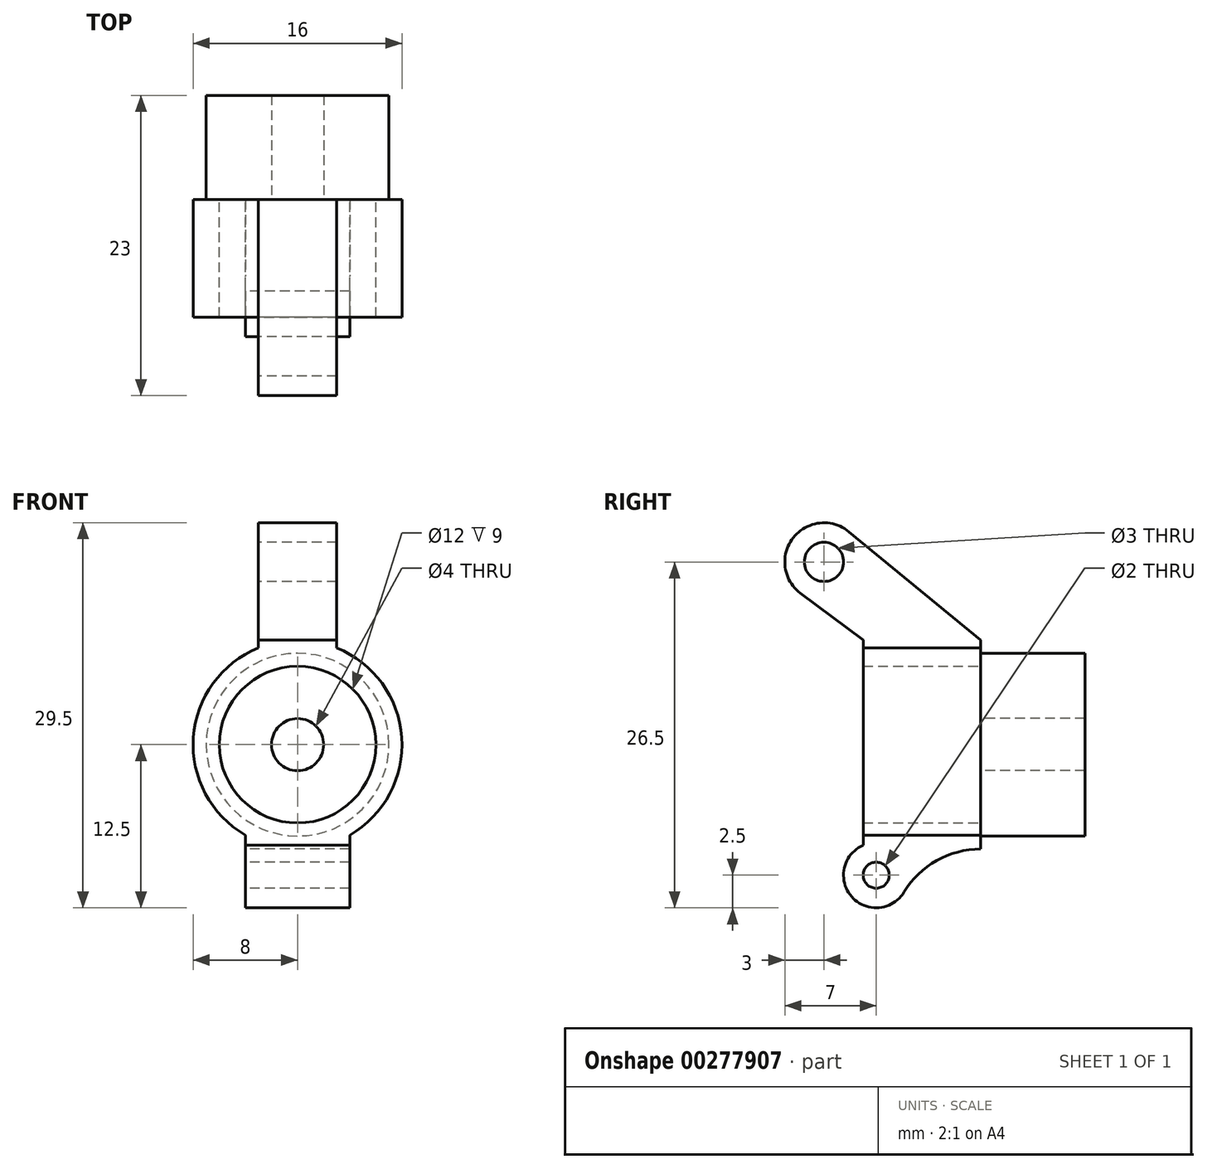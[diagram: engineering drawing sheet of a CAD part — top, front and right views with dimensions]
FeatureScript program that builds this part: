
annotation { "Feature Type Name" : "Feature", "Feature Type Description" : "" }
export const myFeature = defineFeature(function(context is Context, id is Id, definition is map)
    precondition{}
    {
        {
            var Q0;
            Q0=qCreatedBy(makeId("Front.planeOp"),FACE);
            var sketch = newSketch(context, id + "F0", { "sketchPlane" : qUnion([Q0])});
            skArc(sketch, "E0", {"start": v(8, 0) * mm, "mid": v(0, 8) * mm, "end": v(-8, 0) * mm});
            skCircle(sketch, "E1", {"center": v(0, 0) * mm, "radius": 6 * mm});
            skLineSegment(sketch, "E2", {"start": v(0, 0) * mm, "end": v(9.88, 0) * mm, "construction": true});
            skLineSegment(sketch, "E3", {"start": v(0, 0) * mm, "end": v(0, 9.34) * mm, "construction": true});
            skLineSegment(sketch, "E4.MirrorCS", {"start": v(0, 0) * mm, "end": v(-9.88, 0) * mm, "construction": true});
            skArc(sketch, "E5.trimOffspring", {"start": v(-8, 0) * mm, "mid": v(0, -8) * mm, "end": v(8, 0) * mm});
            skPoint(sketch, "E6.end.orphan", {"position": v(7.5, 4) * mm});
            skPoint(sketch, "E6.start.orphan", {"position": v(8, 0) * mm});
            skPoint(sketch, "E7.MirrorCS.end.orphan", {"position": v(7.5, -4) * mm});
            skPoint(sketch, "E8.MirrorCS.start.orphan", {"position": v(-8, 0) * mm});
            skPoint(sketch, "E9.MirrorCS.start.orphan", {"position": v(-7.5, 4) * mm});
            skPoint(sketch, "E10.MirrorCS.start.orphan", {"position": v(-7.5, -4) * mm});
            skSolve(sketch);
        }
        {
            var Q0;
            Q0=qSketchRegion(id+"F0",true);
            extrude(context, id + "F1", {"entities" : qUnion([Q0]), "depth" : 9 * mm, "symmetric" : true});
        }
        {
            var Q0;
            Q0=makeQuery(id+"FDlZR3japZBE9mr_1.boolean.opBoolean","MERGE",FACE,{"derivedFrom":[makeQuery(id+"F1.opExtrude","CAP_FACE",FACE,{"disambiguationData":[OSD([sQuery(id+"F0.wireOp",EDGE,"E0"),sQuery(id+"F0.wireOp",EDGE,"E1"),sQuery(id+"F0.wireOp",EDGE,"E6"),sQuery(id+"F0.wireOp",EDGE,"bKShqBVs-TCg5-hqsg-2Zin-jb4kYLIbsAUQ"),sQuery(id+"F0.wireOp",EDGE,"E8.MirrorCS"),sQuery(id+"F0.wireOp",EDGE,"E9.MirrorCS"),sQuery(id+"F0.wireOp",EDGE,"E7.MirrorCS"),sQuery(id+"F0.wireOp",EDGE,"0079e600-e878-4d57-aa4f-ef33ea1a4fac0.MirrorCS"),sQuery(id+"F0.wireOp",EDGE,"f6fc4373-7105-42fd-a591-3c9390de6fbc0.MirrorCS"),sQuery(id+"F0.wireOp",EDGE,"E10.MirrorCS"),sQuery(id+"F0.wireOp",EDGE,"E5.trimOffspring")])],"isStart":true}),makeQuery(id+"FDlZR3japZBE9mr_1.opExtrude","SWEPT_FACE",FACE,{"disambiguationData":[OSD([sQuery(id+"FTksZrnYcWv5Ukm_1.wireOp",EDGE,"x4EYb6om-VWKb-oGQX-4Byi-Ye5M8WNYVBj3")])]})]});
            var sketch = newSketch(context, id + "F2", { "sketchPlane" : qUnion([Q0])});
            skCircle(sketch, "E11", {"center": v(0, 0) * mm, "radius": 7 * mm});
            skCircle(sketch, "E12", {"center": v(0, 0) * mm, "radius": 2 * mm});
            skSolve(sketch);
        }
        {
            var Q0;
            Q0=qSketchRegion(id+"F2",true);
            extrude(context, id + "F3", {"entities" : qUnion([Q0]), "operationType" : NewBodyOperationType.ADD, "depth" : 8 * mm});
        }
        {
            var Q0;
            Q0=qCreatedBy(makeId("Right.planeOp"),FACE);
            var sketch = newSketch(context, id + "F4", { "sketchPlane" : qUnion([Q0])});
            skCircle(sketch, "E13", {"center": v(-7.5, 14) * mm, "radius": 1.5 * mm});
            skArc(sketch, "E14", {"start": v(-5.6, 16.32) * mm, "mid": v(-9.86, 15.85) * mm, "end": v(-9.3, 11.6) * mm});
            skLineSegment(sketch, "E15", {"start": v(-4.5, 6) * mm, "end": v(-4.5, 8) * mm});
            skLineSegment(sketch, "E16", {"start": v(-4.5, 8) * mm, "end": v(-9.3, 11.6) * mm});
            skLineSegment(sketch, "E17", {"start": v(-5.6, 16.32) * mm, "end": v(4.5, 8) * mm});
            skLineSegment(sketch, "E18", {"start": v(4.5, 8) * mm, "end": v(4.5, 6) * mm});
            skLineSegment(sketch, "E19", {"start": v(4.5, 6) * mm, "end": v(-4.5, 6) * mm});
            skSolve(sketch);
        }
        {
            var Q0;
            Q0 = qSketchRegion(id + "F4", true);
            extrude(context, id + "F5", {"entities" : qUnion([Q0]), "operationType" : NewBodyOperationType.ADD, "depth" : 6 * mm, "symmetric" : true});
        }
        {
            var Q0;
            Q0=qCreatedBy(makeId("Right.planeOp"),FACE);
            var sketch = newSketch(context, id + "F6", { "sketchPlane" : qUnion([Q0])});
            skCircle(sketch, "E20", {"center": v(-3.5, -10) * mm, "radius": 1 * mm});
            skArc(sketch, "E21", {"start": v(-4.5, -7.7) * mm, "mid": v(-5.38, -11.64) * mm, "end": v(-1.36, -11.3) * mm});
            skArc(sketch, "E22", {"start": v(4.5, -8) * mm, "mid": v(1.14, -8.88) * mm, "end": v(-1.36, -11.3) * mm});
            skLineSegment(sketch, "E23", {"start": v(4.5, -8) * mm, "end": v(4.5, -6) * mm});
            skLineSegment(sketch, "E24", {"start": v(4.5, -6) * mm, "end": v(-4.5, -6) * mm});
            skLineSegment(sketch, "E25", {"start": v(-4.5, -6) * mm, "end": v(-4.5, -7.7) * mm});
            skLineSegment(sketch, "E26", {"start": v(4.5, -8) * mm, "end": v(3.66, -8) * mm, "construction": true});
            skSolve(sketch);
        }
        {
            var Q0;
            Q0 = qSketchRegion(id + "F6", true);
            extrude(context, id + "F7", {"entities" : qUnion([Q0]), "operationType" : NewBodyOperationType.ADD, "depth" : 8 * mm, "symmetric" : true});
        }
    });
